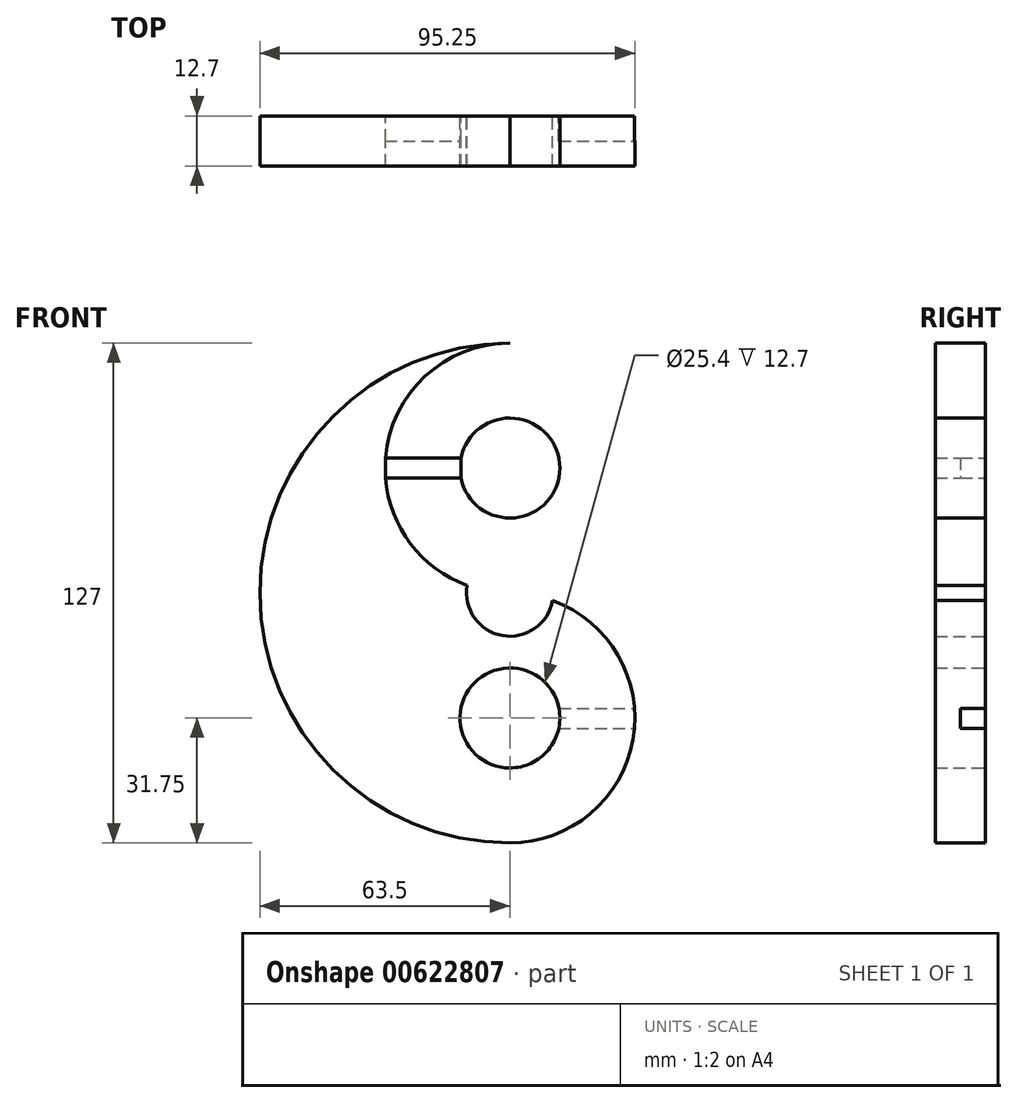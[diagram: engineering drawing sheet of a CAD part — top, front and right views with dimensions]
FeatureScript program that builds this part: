
annotation { "Feature Type Name" : "Feature", "Feature Type Description" : "" }
export const myFeature = defineFeature(function(context is Context, id is Id, definition is map)
    precondition{}
    {
        {
            var Q0;
            Q0=qCreatedBy(makeId("Front.planeOp"),FACE);
            var sketch = newSketch(context, id + "F0", { "sketchPlane" : qUnion([Q0])});
            skArc(sketch, "E0", {"start": v(0, 63.5) * mm, "mid": v(-63.5, 0) * mm, "end": v(0, -63.5) * mm});
            skArc(sketch, "E1", {"start": v(0, -63.5) * mm, "mid": v(31.75, -31.75) * mm, "end": v(0, 0) * mm});
            skArc(sketch, "E2.2.0", {"start": v(0, 63.5) * mm, "mid": v(-21.53, 55.08) * mm, "end": v(-31.65, 34.3) * mm});
            skLineSegment(sketch, "E2.anchor1", {"start": v(0, 0) * mm, "end": v(0, -63.5) * mm, "construction": true});
            skLineSegment(sketch, "E2.anchor2", {"start": v(0, 0) * mm, "end": v(0, 63.5) * mm, "construction": true});
            skArc(sketch, "E3", {"start": v(-12.44, 29.21) * mm, "mid": v(12.7, 31.75) * mm, "end": v(-12.44, 34.3) * mm});
            skCircle(sketch, "E4", {"center": v(0, -31.75) * mm, "radius": 12.7 * mm});
            skLineSegment(sketch, "E5.bottom", {"start": v(-31.65, 34.3) * mm, "end": v(-12.44, 34.3) * mm});
            skLineSegment(sketch, "E5.top", {"start": v(-31.65, 29.21) * mm, "end": v(-12.44, 29.21) * mm});
            skArc(sketch, "E6.trimOffspring", {"start": v(-31.65, 29.2) * mm, "mid": v(-21.53, 8.42) * mm, "end": v(0, 0) * mm});
            skSolve(sketch);
        }
        {
            var Q0;
            Q0=makeQuery(id+"F0.imprint","IMPRINT",FACE,{"disambiguationData":[TD([[makeQuery(id+"F0.imprint","IMPRINT",EDGE,{"derivedFrom":sQuery(id+"F0.wireOp",EDGE,"E0")}),1.0]])]});
            extrude(context, id + "F1", {"entities" : qUnion([Q0]), "depth" : 12.7 * mm, "offsetDistance" : 25.4 * mm});
        }
        {
            var Q0;
            Q0=makeQuery(id+"F1.opExtrude","CAP_FACE",FACE,{"disambiguationData":[OSD([sQuery(id+"F0.wireOp",EDGE,"E0"),sQuery(id+"F0.wireOp",EDGE,"E1"),sQuery(id+"F0.wireOp",EDGE,"E2.2.0"),sQuery(id+"F0.wireOp",EDGE,"E3"),sQuery(id+"F0.wireOp",EDGE,"E4"),sQuery(id+"F0.wireOp",EDGE,"E5.bottom"),sQuery(id+"F0.wireOp",EDGE,"E5.top"),sQuery(id+"F0.wireOp",EDGE,"E6.trimOffspring")])],"isStart":true});
            var sketch = newSketch(context, id + "F2", { "sketchPlane" : qUnion([Q0])});
            skLineSegment(sketch, "E7.bottom", {"start": v(-12.41, -29.37) * mm, "end": v(-34.23, -29.37) * mm});
            skLineSegment(sketch, "E7.top", {"start": v(-12.41, -34.45) * mm, "end": v(-34.23, -34.45) * mm});
            skLineSegment(sketch, "E7.left", {"start": v(-12.41, -29.37) * mm, "end": v(-12.41, -34.45) * mm});
            skLineSegment(sketch, "E7.right", {"start": v(-34.23, -29.37) * mm, "end": v(-34.23, -34.45) * mm});
            skSolve(sketch);
        }
        {
            var Q0;
            {var subQ0=sQuery(id+"F2.wireOp",EDGE,"E7.bottom");var subQ1=makeQuery(id+"F1.opExtrude","CAP_EDGE",EDGE,{"disambiguationData":[OSD([sQuery(id+"F0.wireOp",EDGE,"E1")])],"isStart":true});var subQ2=makeQuery(id+"F2.imprint","INTERSECT",VERTEX,{"derivedFrom":[subQ1,subQ0]});Q0=makeQuery(id+"F2.imprint","IMPRINT",FACE,{"disambiguationData":[TD([[makeQuery(id+"F2.imprint","IMPRINT",EDGE,{"disambiguationData":[TD([[subQ2,1.0]])],"derivedFrom":subQ0}),1.0]])]});}
            extrude(context, id + "F3", {"entities" : qUnion([Q0]), "operationType" : NewBodyOperationType.REMOVE, "oppositeDirection" : true, "depth" : 6.35 * mm, "offsetDistance" : 25.4 * mm});
        }
        {
            var Q0;
            Q0=makeQuery(id+"F1.opExtrude","CAP_FACE",FACE,{"disambiguationData":[OSD([sQuery(id+"F0.wireOp",EDGE,"E0"),sQuery(id+"F0.wireOp",EDGE,"E1"),sQuery(id+"F0.wireOp",EDGE,"E2.2.0"),sQuery(id+"F0.wireOp",EDGE,"E3"),sQuery(id+"F0.wireOp",EDGE,"E4"),sQuery(id+"F0.wireOp",EDGE,"E5.bottom"),sQuery(id+"F0.wireOp",EDGE,"E5.top"),sQuery(id+"F0.wireOp",EDGE,"E6.trimOffspring")])],"isStart":false});
            var sketch = newSketch(context, id + "F4", { "sketchPlane" : qUnion([Q0])});
            skLineSegment(sketch, "E8.bottom", {"start": v(-31.65, 34.3) * mm, "end": v(-12.44, 34.3) * mm});
            skLineSegment(sketch, "E8.top", {"start": v(-31.65, 29.21) * mm, "end": v(-12.44, 29.21) * mm});
            skLineSegment(sketch, "E8.left", {"start": v(-31.65, 34.3) * mm, "end": v(-31.65, 29.21) * mm});
            skLineSegment(sketch, "E8.right", {"start": v(-12.44, 34.3) * mm, "end": v(-12.44, 29.21) * mm});
            skSolve(sketch);
        }
        {
            var Q0;
            Q0=makeQuery(id+"F4.imprint","IMPRINT",FACE,{"disambiguationData":[TD([[makeQuery(id+"F4.imprint","IMPRINT",EDGE,{"derivedFrom":sQuery(id+"F4.wireOp",EDGE,"E8.bottom")}),-1.0]])]});
            extrude(context, id + "F5", {"entities" : qUnion([Q0]), "operationType" : NewBodyOperationType.REMOVE, "oppositeDirection" : true, "depth" : 6.35 * mm, "offsetDistance" : 25.4 * mm});
        }
        {
            var Q0;
            Q0=makeQuery(id+"F1.opExtrude","CAP_FACE",FACE,{"disambiguationData":[OSD([sQuery(id+"F0.wireOp",EDGE,"E0"),sQuery(id+"F0.wireOp",EDGE,"E1"),sQuery(id+"F0.wireOp",EDGE,"E2.2.0"),sQuery(id+"F0.wireOp",EDGE,"E3"),sQuery(id+"F0.wireOp",EDGE,"E4"),sQuery(id+"F0.wireOp",EDGE,"E5.bottom"),sQuery(id+"F0.wireOp",EDGE,"E5.top"),sQuery(id+"F0.wireOp",EDGE,"E6.trimOffspring")])],"isStart":true});
            var sketch = newSketch(context, id + "F6", { "sketchPlane" : qUnion([Q0])});
            skCircle(sketch, "E9", {"center": v(0, 0) * mm, "radius": 11 * mm});
            skSolve(sketch);
        }
        {
            var Q0;
            {var subQ0=sQuery(id+"F6.wireOp",EDGE,"E9");var subQ1=sQuery(id+"F0.wireOp",EDGE,"E6.trimOffspring");var subQ2=makeQuery(id+"F1.opExtrude","CAP_EDGE",EDGE,{"disambiguationData":[OSD([subQ1])],"isStart":true});var subQ3=makeQuery(id+"F6.imprint","INTERSECT",VERTEX,{"derivedFrom":[subQ2,subQ0]});Q0=makeQuery(id+"F6.imprint","IMPRINT",FACE,{"disambiguationData":[TD([[makeQuery(id+"F6.imprint","IMPRINT",EDGE,{"disambiguationData":[TD([[subQ3,1.0]])],"derivedFrom":subQ0}),1.0]])]});}
            extrude(context, id + "F7", {"entities" : qUnion([Q0]), "operationType" : NewBodyOperationType.REMOVE, "oppositeDirection" : true, "depth" : 25.4 * mm, "offsetDistance" : 25.4 * mm});
        }
    });
